FCSTD DOCUMENT  (FreeCAD 0.18R15705 (Git))
Label: Coilcraft_LPS5030
License: All rights reserved
LicenseURL: http://en.wikipedia.org/wiki/All_rights_reserved
objects: Sketcher::SketchObject×4, App::Annotation×2, App::DocumentObjectGroup×1
note: 4 computed .brp shape members not serialized (recipe doc carries the construction recipe); baked Part::Feature solids carry a one-line shape summary decoded from their .brp

FEATURE [Sketcher::SketchObject] Sketch004  label="F_Fab_0.1"
  sketch-geometry (12):
    g0: LineSegment StartX=-1.4 StartY=2.4 StartZ=0 EndX=1.4 EndY=2.4 EndZ=0
    g1: LineSegment StartX=2.4 StartY=1.4 StartZ=0 EndX=2.4 EndY=-1.4 EndZ=0
    g2: LineSegment StartX=1.4 StartY=-2.4 StartZ=0 EndX=-1.4 EndY=-2.4 EndZ=0
    g3: LineSegment StartX=-2.4 StartY=-1.4 StartZ=0 EndX=-2.4 EndY=1.4 EndZ=0
    g4: LineSegment StartX=-2.4 StartY=1.4 StartZ=0 EndX=-1.4 EndY=2.4 EndZ=0
    g5: LineSegment StartX=1.4 StartY=2.4 StartZ=0 EndX=2.4 EndY=1.4 EndZ=0
    g6: LineSegment StartX=2.4 StartY=-1.4 StartZ=0 EndX=1.4 EndY=-2.4 EndZ=0
    g7: LineSegment StartX=-2.4 StartY=-1.4 StartZ=0 EndX=-1.4 EndY=-2.4 EndZ=0
    g8: LineSegment [constr] StartX=-2.4 StartY=2.4 StartZ=0 EndX=2.4 EndY=2.4 EndZ=0
    g9: LineSegment [constr] StartX=2.4 StartY=2.4 StartZ=0 EndX=2.4 EndY=-2.4 EndZ=0
    g10: LineSegment [constr] StartX=2.4 StartY=-2.4 StartZ=0 EndX=-2.4 EndY=-2.4 EndZ=0
    g11: LineSegment [constr] StartX=-2.4 StartY=-2.4 StartZ=0 EndX=-2.4 EndY=2.4 EndZ=0
  constraints (34):
    c: Vertical(g3)
    c: Coincident(g0,g4)
    c: Coincident(g3,g4)
    c: Coincident(g0,g5)
    c: Coincident(g1,g5)
    c: Coincident(g1,g6)
    c: Coincident(g2,g6)
    c: Coincident(g2,g7)
    c: Coincident(g3,g7)
    c: Coincident(g8,g9)
    c: Coincident(g9,g10)
    c: Coincident(g10,g11)
    c: Coincident(g11,g8)
    c: Horizontal(g10)
    c: Vertical(g11)
    c: Symmetric(g8,g8,g-2)
    c: Symmetric(g8,g9,g-1)
    c: Equal(g8,g9)
    c: DistanceX(g8,g8) = 4.8
    c: PointOnObject(g0,g8)
    c: PointOnObject(g0,g8)
    c: PointOnObject(g3,g11)
    c: PointOnObject(g2,g10)
    c: PointOnObject(g2,g10)
    c: PointOnObject(g1,g9)
    c: Equal(g1,g0)
    c: Equal(g0,g3)
    c: Equal(g3,g2)
    c: Equal(g6,g7)
    c: Equal(g7,g4)
    c: Equal(g4,g5)
    c: PointOnObject(g1,g9)
    c: DistanceX(g8,g0) = 1
    c: DistanceY(g4,g4) = 1
FEATURE [App::Annotation] Text  label="Ref#_1.0mm"
  LabelText = REF**
  Position = (0,4,0)
FEATURE [App::Annotation] Text001  label="Value#_0.8mm"
  LabelText = Value 
  Position = (0,-5.5,0)
FEATURE [Sketcher::SketchObject] Sketch011  label="Pads_Poly"
  expr: Constraints[24] = 3.3999999999999999 / 2
  expr: Constraints[23] = 5.5099999999999998 / 2
  expr: Constraints[22] = 1.52 / 2
  expr: Constraints[21] = 3.3999999999999999 / 2
  sketch-geometry (22):
    g0: LineSegment StartX=-0.76 StartY=2.755 StartZ=0 EndX=-0.76 EndY=1.7 EndZ=0
    g1: LineSegment StartX=-0.76 StartY=1.7 StartZ=0 EndX=-1.7 EndY=0.8445 EndZ=0
    g2: LineSegment StartX=-1.7 StartY=0.8445 StartZ=0 EndX=-1.7 EndY=-0.8445 EndZ=0
    g3: LineSegment StartX=-1.7 StartY=-0.8445 StartZ=0 EndX=-0.76 EndY=-1.7 EndZ=0
    g4: LineSegment StartX=-0.76 StartY=-1.7 StartZ=0 EndX=-0.76 EndY=-2.755 EndZ=0
    g5: LineSegment StartX=-0.76 StartY=-2.755 StartZ=0 EndX=-1.7 EndY=-2.755 EndZ=0
    g6: LineSegment StartX=-1.7 StartY=-2.755 StartZ=0 EndX=-2.755 EndY=-1.7 EndZ=0
    g7: LineSegment StartX=-2.755 StartY=-1.7 StartZ=0 EndX=-2.755 EndY=1.7 EndZ=0
    g8: LineSegment StartX=-2.755 StartY=1.7 StartZ=0 EndX=-1.7 EndY=2.755 EndZ=0
    g9: LineSegment StartX=-1.7 StartY=2.755 StartZ=0 EndX=-0.76 EndY=2.755 EndZ=0
    g10: Circle CenterX=-2.2275 CenterY=0 CenterZ=0 NormalX=0 NormalY=0 NormalZ=1 AngleXU=0 Radius=0.5275
    g11: LineSegment StartX=0.76 StartY=2.755 StartZ=0 EndX=0.76 EndY=1.7 EndZ=0
    g12: LineSegment StartX=0.76 StartY=1.7 StartZ=0 EndX=1.7 EndY=0.8445 EndZ=0
    g13: LineSegment StartX=1.7 StartY=0.8445 StartZ=0 EndX=1.7 EndY=-0.8445 EndZ=0
    g14: LineSegment StartX=1.7 StartY=-0.8445 StartZ=0 EndX=0.76 EndY=-1.7 EndZ=0
    g15: LineSegment StartX=0.76 StartY=-1.7 StartZ=0 EndX=0.76 EndY=-2.755 EndZ=0
    g16: LineSegment StartX=0.76 StartY=-2.755 StartZ=0 EndX=1.7 EndY=-2.755 EndZ=0
    g17: LineSegment StartX=1.7 StartY=-2.755 StartZ=0 EndX=2.755 EndY=-1.7 EndZ=0
    g18: LineSegment StartX=2.755 StartY=-1.7 StartZ=0 EndX=2.755 EndY=1.7 EndZ=0
    g19: LineSegment StartX=2.755 StartY=1.7 StartZ=0 EndX=1.7 EndY=2.755 EndZ=0
    g20: LineSegment StartX=1.7 StartY=2.755 StartZ=0 EndX=0.76 EndY=2.755 EndZ=0
    g21: Circle CenterX=2.2275 CenterY=0 CenterZ=0 NormalX=0 NormalY=0 NormalZ=1 AngleXU=0 Radius=0.5275
  constraints (59):
    c: Coincident(g0,g1)
    c: Coincident(g1,g2)
    c: Coincident(g2,g3)
    c: Coincident(g3,g4)
    c: Coincident(g4,g5)
    c: Coincident(g5,g6)
    c: Coincident(g6,g7)
    c: Coincident(g7,g8)
    c: Coincident(g8,g9)
    c: Coincident(g9,g0)
    c: Horizontal(g9)
    c: Horizontal(g5)
    c: Vertical(g0)
    c: Vertical(g4)
    c: DistanceY(g2,g2) = 1.689
    c: Symmetric(g2,g1,g-1)
    c: Symmetric(g0,g3,g-1)
    c: Symmetric(g7,g6,g-1)
    c: Symmetric(g5,g8,g-1)
    c: DistanceY(g4,g0) = 5.51
    c: DistanceY(g3,g0) = 3.4
    c: DistanceX(g1,g-1) = 1.7
    c: DistanceX(g0,g-1) = 0.76
    c: DistanceX(g7,g-1) = 2.755
    c: DistanceX(g8,g-1) = 1.7
    c: PointOnObject(g10,g-1)
    c: Tangent(g10,g7)
    c: Tangent(g10,g2)
    c: DistanceY(g7,g7) = 3.4
    c: Coincident(g11,g12)
    c: Coincident(g12,g13)
    c: Coincident(g13,g14)
    c: Coincident(g14,g15)
    c: Coincident(g15,g16)
    c: Coincident(g16,g17)
    c: Coincident(g17,g18)
    c: Coincident(g18,g19)
    c: Coincident(g19,g20)
    c: Coincident(g20,g11)
    c: Horizontal(g16)
    c: Vertical(g11)
    c: Vertical(g15)
    c: Tangent(g21,g18)
    c: Tangent(g21,g13)
    c: Equal(g4,g15)
    c: Equal(g16,g5)
    c: Equal(g14,g3)
    c: Equal(g6,g17)
    c: Equal(g13,g2)
    c: Equal(g12,g1)
    c: Equal(g11,g0)
    c: Equal(g20,g9)
    c: Equal(g19,g8)
    c: Equal(g7,g18)
    c: Symmetric(g11,g0,g-2)
    c: Symmetric(g18,g7,g-2)
    c: Vertical(g13)
    c: PointOnObject(g21,g-1)
    c: Symmetric(g15,g4,g-2)
FEATURE [Sketcher::SketchObject] Sketch002  label="F_CrtYd_0.05"
  ExternalGeometry = -> [Sketch011]
  sketch-geometry (13):
    g0: LineSegment StartX=-3.01 StartY=1.8 StartZ=0 EndX=-1.8 EndY=3.01 EndZ=0
    g1: LineSegment StartX=-1.8 StartY=3.01 StartZ=0 EndX=1.8 EndY=3.01 EndZ=0
    g2: LineSegment StartX=1.8 StartY=3.01 StartZ=0 EndX=3.01 EndY=1.8 EndZ=0
    g3: LineSegment StartX=3.01 StartY=1.8 StartZ=0 EndX=3.01 EndY=-1.8 EndZ=0
    g4: LineSegment StartX=3.01 StartY=-1.8 StartZ=0 EndX=1.8 EndY=-3.01 EndZ=0
    g5: LineSegment StartX=1.8 StartY=-3.01 StartZ=0 EndX=-1.8 EndY=-3.01 EndZ=0
    g6: LineSegment StartX=-1.8 StartY=-3.01 StartZ=0 EndX=-3.01 EndY=-1.8 EndZ=0
    g7: LineSegment StartX=-3.01 StartY=-1.8 StartZ=0 EndX=-3.01 EndY=1.8 EndZ=0
    g8: LineSegment [constr] StartX=-1.8 StartY=3.01 StartZ=0 EndX=-1.6225 EndY=2.8325 EndZ=0
    g9: LineSegment [constr] StartX=-3.01 StartY=3.01 StartZ=0 EndX=3.01 EndY=3.01 EndZ=0
    g10: LineSegment [constr] StartX=3.01 StartY=3.01 StartZ=0 EndX=3.01 EndY=-3.01 EndZ=0
    g11: LineSegment [constr] StartX=3.01 StartY=-3.01 StartZ=0 EndX=-3.01 EndY=-3.01 EndZ=0
    g12: LineSegment [constr] StartX=-3.01 StartY=-3.01 StartZ=0 EndX=-3.01 EndY=3.01 EndZ=0
  constraints (38):
    c: Coincident(g0,g1)
    c: Coincident(g1,g2)
    c: Coincident(g2,g3)
    c: Vertical(g3)
    c: Coincident(g3,g4)
    c: Coincident(g4,g5)
    c: Horizontal(g5)
    c: Coincident(g5,g6)
    c: Coincident(g6,g7)
    c: Coincident(g7,g0)
    c: Vertical(g7)
    c: Equal(g0,g2)
    c: Equal(g2,g4)
    c: Equal(g4,g6)
    c: Equal(g3,g1)
    c: Equal(g1,g7)
    c: Equal(g7,g5)
    c: PointOnObject(g8,g-3)
    c: Perpendicular(g-3,g8)
    c: Coincident(g8,g0)
    c: Coincident(g9,g10)
    c: Coincident(g10,g11)
    c: Coincident(g11,g12)
    c: Coincident(g12,g9)
    c: Horizontal(g11)
    c: Vertical(g12)
    c: Equal(g10,g9)
    c: Symmetric(g9,g9,g-2)
    c: Symmetric(g10,g9,g-1)
    c: DistanceX(g9,g-3) = 0.255
    c: DistanceX(g9,g-1) = 3.01
    c: PointOnObject(g0,g12)
    c: PointOnObject(g0,g9)
    c: PointOnObject(g2,g10)
    c: PointOnObject(g4,g11)
    c: Symmetric(g1,g0,g-2)
    c: DistanceX(g0,g-1) = 1.8
    c: Distance(g8) = 0.251023
FEATURE [Sketcher::SketchObject] Sketch003  label="F_Silks_0.12"
  ExternalGeometry = -> [Sketch011,Sketch004]
  expr: Constraints[4] = 0.20000000000000001 + 0.12 / 2
  sketch-geometry (2):
    g0: LineSegment StartX=-0.5 StartY=2.51 StartZ=0 EndX=0.5 EndY=2.51 EndZ=0
    g1: LineSegment StartX=-0.5 StartY=-2.51 StartZ=0 EndX=0.5 EndY=-2.51 EndZ=0
  constraints (5):
    c: Symmetric(g1,g1,g-2)
    c: Symmetric(g1,g0,g-1)
    c: Symmetric(g1,g0,g-1)
    c: DistanceY(g1,g-4) = 0.11
    c: DistanceX(g-3,g1) = 0.26
FEATURE [App::DocumentObjectGroup] Group  label="L_Coilcraft_LPS5030"
  Group = -> [Sketch002,Sketch003,Sketch004,Sketch011,Text,Text001]
